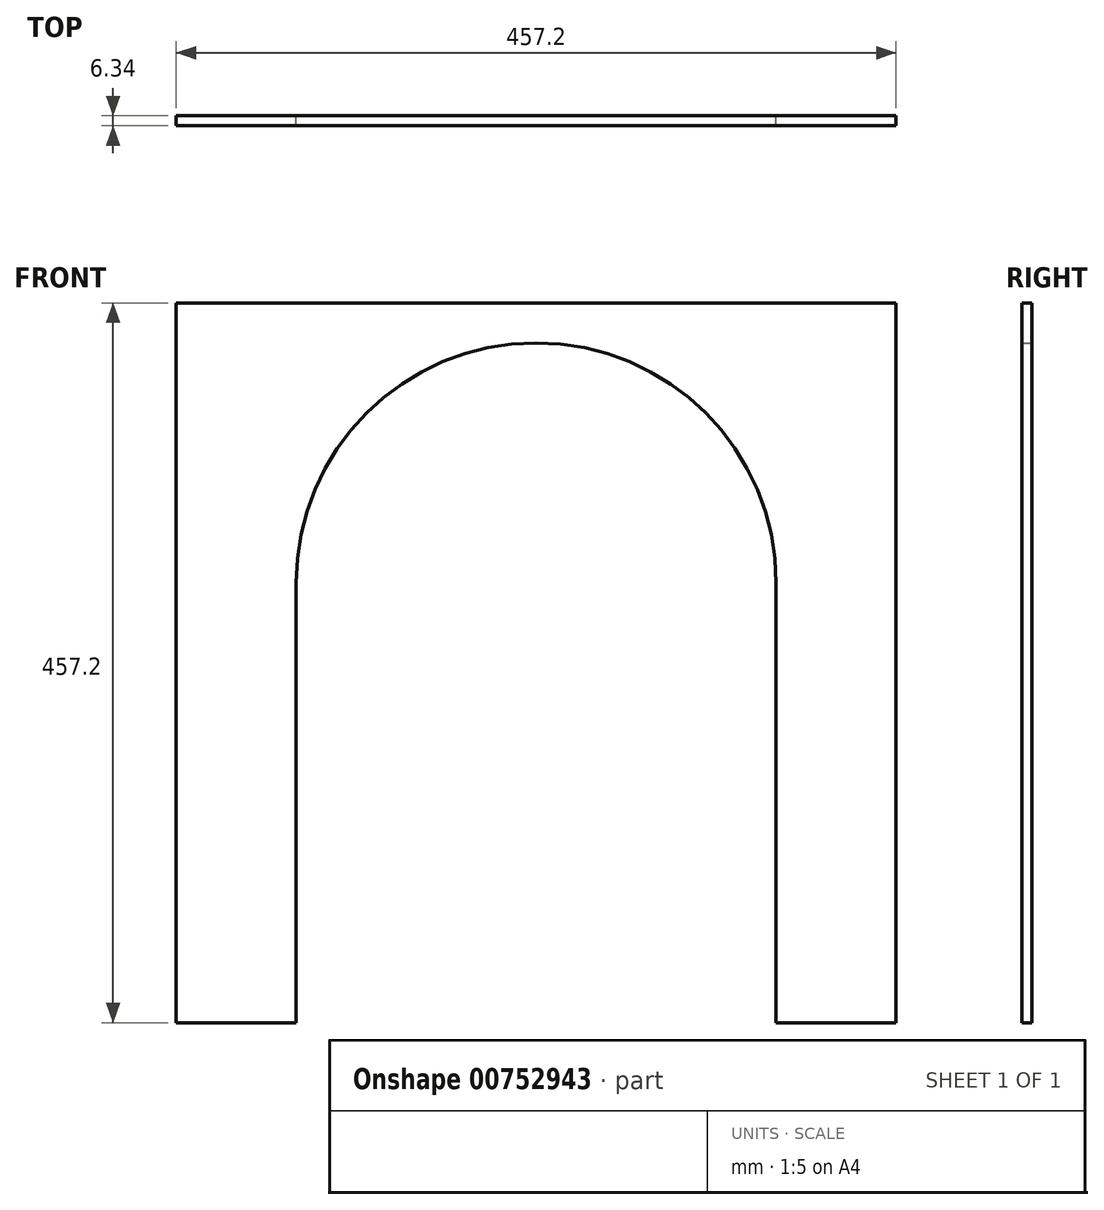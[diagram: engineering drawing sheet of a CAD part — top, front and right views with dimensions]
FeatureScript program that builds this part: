
annotation { "Feature Type Name" : "Feature", "Feature Type Description" : "" }
export const myFeature = defineFeature(function(context is Context, id is Id, definition is map)
    precondition{}
    {
        {
            var Q0;
            Q0=qCreatedBy(makeId("Front.planeOp"),FACE);
            var sketch = newSketch(context, id + "F0", { "sketchPlane" : qUnion([Q0])});
            skLineSegment(sketch, "E0.bottom", {"start": v(0, 0) * mm, "end": v(457.2, 0) * mm});
            skLineSegment(sketch, "E0.top", {"start": v(0, 457.2) * mm, "end": v(457.2, 457.2) * mm});
            skLineSegment(sketch, "E0.left", {"start": v(0, 0) * mm, "end": v(0, 457.2) * mm});
            skLineSegment(sketch, "E0.right", {"start": v(457.2, 0) * mm, "end": v(457.2, 457.2) * mm});
            skLineSegment(sketch, "E1", {"start": v(76.2, 0) * mm, "end": v(76.2, 279.4) * mm});
            skLineSegment(sketch, "E2", {"start": v(381, 0) * mm, "end": v(381, 279.4) * mm});
            skArc(sketch, "E3", {"start": v(381, 279.4) * mm, "mid": v(228.6, 431.8) * mm, "end": v(76.2, 279.4) * mm});
            skSolve(sketch);
        }
        {
            var Q0;
            Q0=makeQuery(id+"F0.imprint","IMPRINT",FACE,{"disambiguationData":[TD([[makeQuery(id+"F0.imprint","IMPRINT",EDGE,{"derivedFrom":sQuery(id+"F0.wireOp",EDGE,"E0.top")}),-1.0]])]});
            extrude(context, id + "F1", {"entities" : qUnion([Q0]), "depth" : 6.35 * mm, "offsetDistance" : 25.4 * mm, "symmetric" : true});
        }
    });
